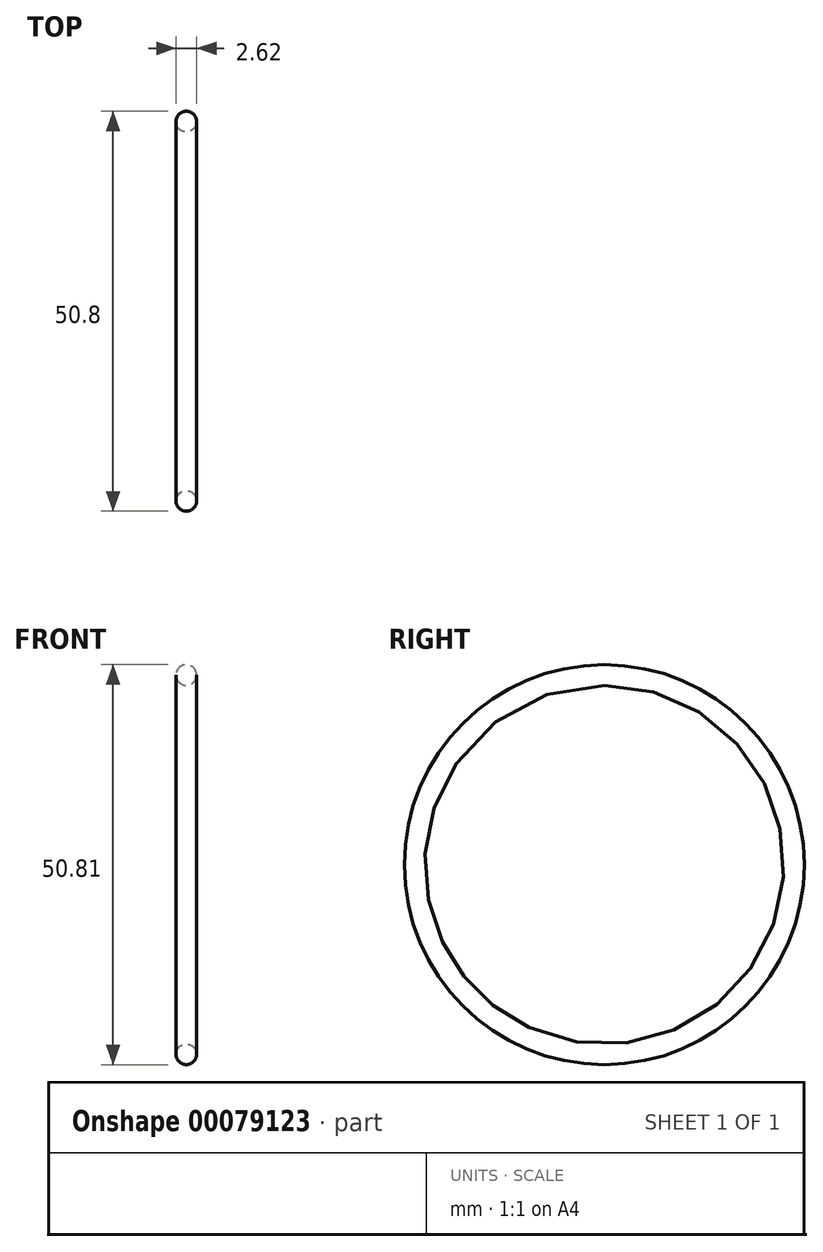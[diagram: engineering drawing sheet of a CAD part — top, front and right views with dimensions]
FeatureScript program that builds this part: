
annotation { "Feature Type Name" : "Feature", "Feature Type Description" : "" }
export const myFeature = defineFeature(function(context is Context, id is Id, definition is map)
    precondition{}
    {
        {
            var Q0;
            Q0=qCreatedBy(makeId("Front.planeOp"),FACE);
            var sketch = newSketch(context, id + "F0", { "sketchPlane" : qUnion([Q0])});
            skCircle(sketch, "E0", {"center": v(0, 24.1) * mm, "radius": 1.3 * mm});
            skLineSegment(sketch, "E1", {"start": v(-0.15, 0) * mm, "end": v(4.27, 0) * mm});
            skSolve(sketch);
        }
        {
            var Q0;
            Q0=makeQuery(id+"F0.imprint","IMPRINT",FACE,{"disambiguationData":[TD([[makeQuery(id+"F0.imprint","IMPRINT",EDGE,{"derivedFrom":sQuery(id+"F0.wireOp",EDGE,"E0")}),1.0]])]});
            var Q1;
            Q1=sQuery(id+"F0.wireOp",EDGE,"E1");
            revolve(context, id + "F1", {"entities" : qUnion([Q0]), "axis" : qUnion([Q1]), "revolveType" : RevolveType.FULL});
        }
    });
